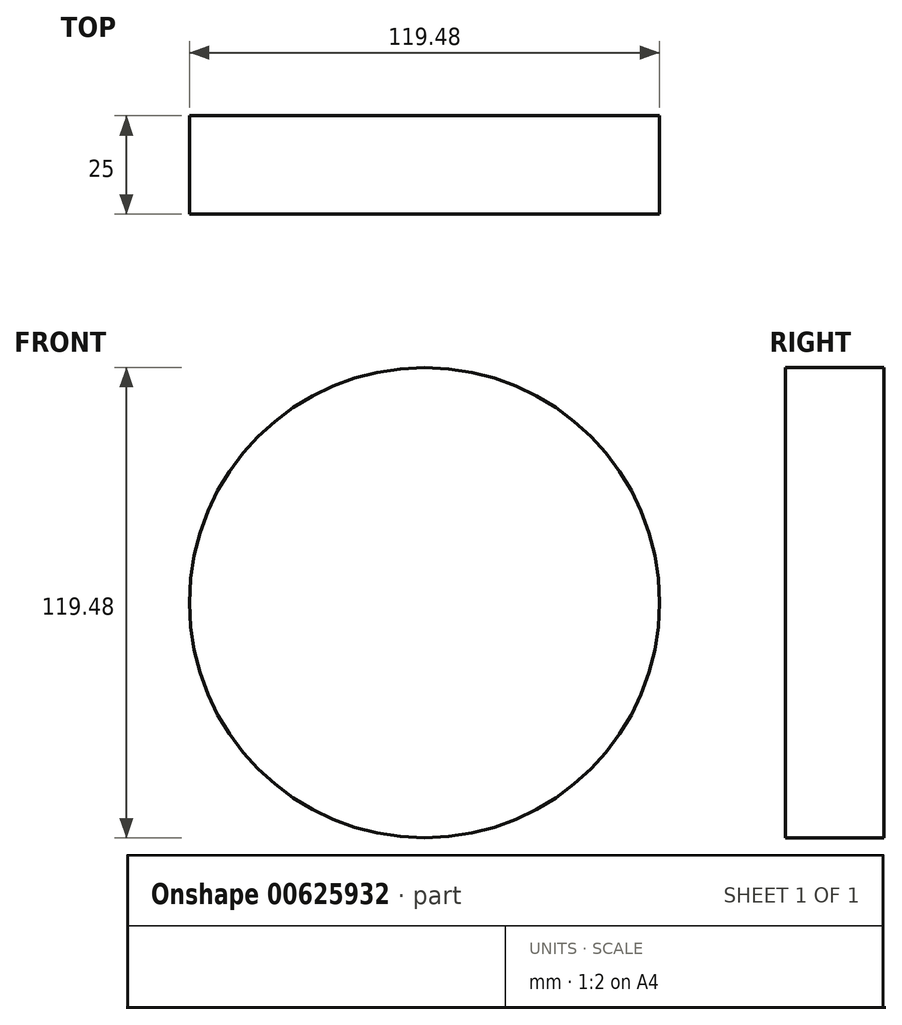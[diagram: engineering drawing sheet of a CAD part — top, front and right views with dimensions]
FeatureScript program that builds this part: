
annotation { "Feature Type Name" : "Feature", "Feature Type Description" : "" }
export const myFeature = defineFeature(function(context is Context, id is Id, definition is map)
    precondition{}
    {
        {
            var Q0;
            Q0=qCreatedBy(makeId("Front.planeOp"),FACE);
            var sketch = newSketch(context, id + "F0", { "sketchPlane" : qUnion([Q0])});
            skCircle(sketch, "E0", {"center": v(0, 0) * mm, "radius": 59.74 * mm});
            skCircle(sketch, "E1", {"center": v(0, 0) * mm, "radius": 75.86 * mm});
            skSolve(sketch);
        }
        {
            var Q0;
            Q0=makeQuery(id+"F0.imprint","IMPRINT",FACE,{"disambiguationData":[TD([[makeQuery(id+"F0.imprint","IMPRINT",EDGE,{"derivedFrom":sQuery(id+"F0.wireOp",EDGE,"E0")}),1.0]])]});
            extrude(context, id + "F1", {"entities" : qUnion([Q0]), "depth" : 25 * mm, "offsetDistance" : 25 * mm});
        }
    });
